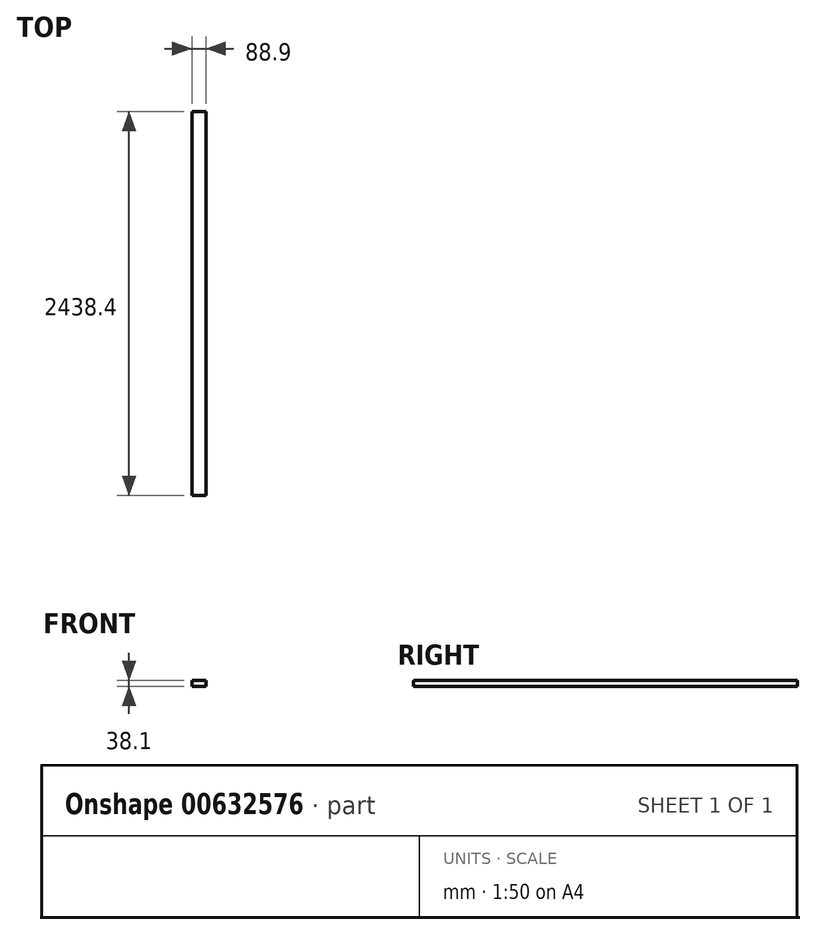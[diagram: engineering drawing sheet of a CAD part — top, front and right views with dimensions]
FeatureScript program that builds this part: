
annotation { "Feature Type Name" : "Feature", "Feature Type Description" : "" }
export const myFeature = defineFeature(function(context is Context, id is Id, definition is map)
    precondition{}
    {
        {
            var Q0;
            Q0=qCreatedBy(makeId("Top.planeOp"),FACE);
            var sketch = newSketch(context, id + "F0", { "sketchPlane" : qUnion([Q0])});
            skLineSegment(sketch, "E0.bottom", {"start": v(-13.04, 2378.84) * mm, "end": v(75.86, 2378.84) * mm});
            skLineSegment(sketch, "E0.top", {"start": v(-13.04, -59.56) * mm, "end": v(75.86, -59.56) * mm});
            skLineSegment(sketch, "E0.left", {"start": v(-13.04, 2378.84) * mm, "end": v(-13.04, -59.56) * mm});
            skLineSegment(sketch, "E0.right", {"start": v(75.86, 2378.84) * mm, "end": v(75.86, -59.56) * mm});
            skSolve(sketch);
        }
        {
            var Q0;
            Q0 = qSketchRegion(id + "F0", true);
            extrude(context, id + "F1", {"entities" : qUnion([Q0]), "depth" : 38.1 * mm, "offsetDistance" : 25.4 * mm});
        }
    });
